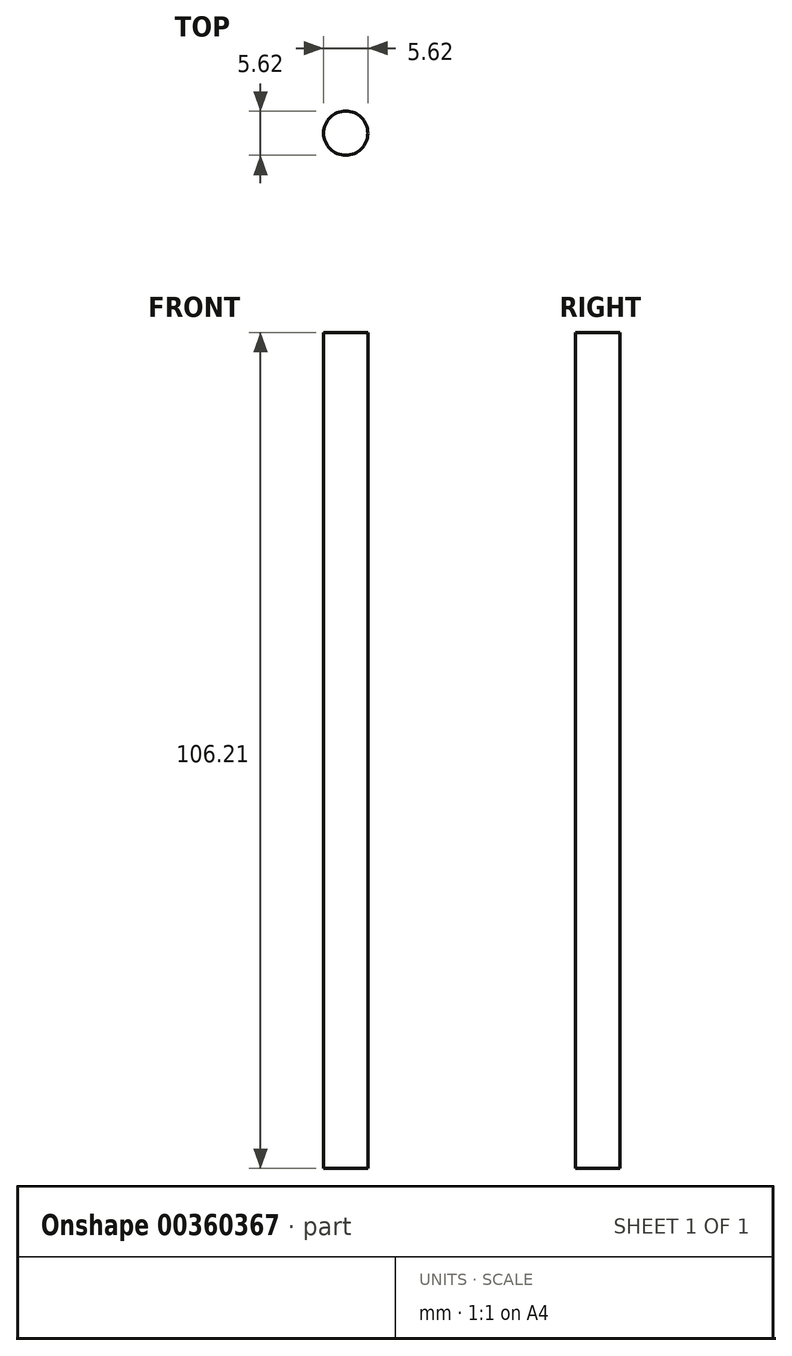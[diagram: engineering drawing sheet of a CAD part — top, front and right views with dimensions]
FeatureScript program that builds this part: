
annotation { "Feature Type Name" : "Feature", "Feature Type Description" : "" }
export const myFeature = defineFeature(function(context is Context, id is Id, definition is map)
    precondition{}
    {
        {
            var Q0;
            Q0=qCreatedBy(makeId("Right.planeOp"),FACE);
            var sketch = newSketch(context, id + "F0", { "sketchPlane" : qUnion([Q0])});
            skLineSegment(sketch, "E0", {"start": v(-47.9, 48.5) * mm, "end": v(-47.9, -57.7) * mm});
            skLineSegment(sketch, "E1", {"start": v(-47.9, -57.7) * mm, "end": v(-45.08, -57.7) * mm});
            skLineSegment(sketch, "E2", {"start": v(-45.08, 48.5) * mm, "end": v(-47.9, 48.5) * mm});
            skLineSegment(sketch, "E3", {"start": v(-45.08, 48.5) * mm, "end": v(-45.08, -57.7) * mm});
            skPoint(sketch, "E4.orphan", {"position": v(-42.27, 48.5) * mm});
            skPoint(sketch, "E5.orphan", {"position": v(-42.27, -57.7) * mm});
            skLineSegment(sketch, "E6.MirrorCS", {"start": v(45.08, 48.5) * mm, "end": v(45.08, -57.7) * mm});
            skLineSegment(sketch, "E7.MirrorCS", {"start": v(47.9, 48.5) * mm, "end": v(47.9, -57.7) * mm});
            skLineSegment(sketch, "E8.MirrorCS", {"start": v(45.08, 48.5) * mm, "end": v(47.9, 48.5) * mm});
            skLineSegment(sketch, "E9.MirrorCS", {"start": v(47.9, -57.7) * mm, "end": v(45.08, -57.7) * mm});
            skSolve(sketch);
        }
        {
            var Q0;
            Q0=makeQuery(id+"F0.imprint","IMPRINT",FACE,{"disambiguationData":[TD([[makeQuery(id+"F0.imprint","IMPRINT",EDGE,{"derivedFrom":sQuery(id+"F0.wireOp",EDGE,"E6.MirrorCS")}),1.0]])]});
            var Q1;
            Q1=sQuery(id+"F0.wireOp",EDGE,"E6.MirrorCS");
            revolve(context, id + "F1", {"entities" : qUnion([Q0]), "axis" : qUnion([Q1]), "revolveType" : RevolveType.FULL, "oppositeDirection" : true});
        }
    });
